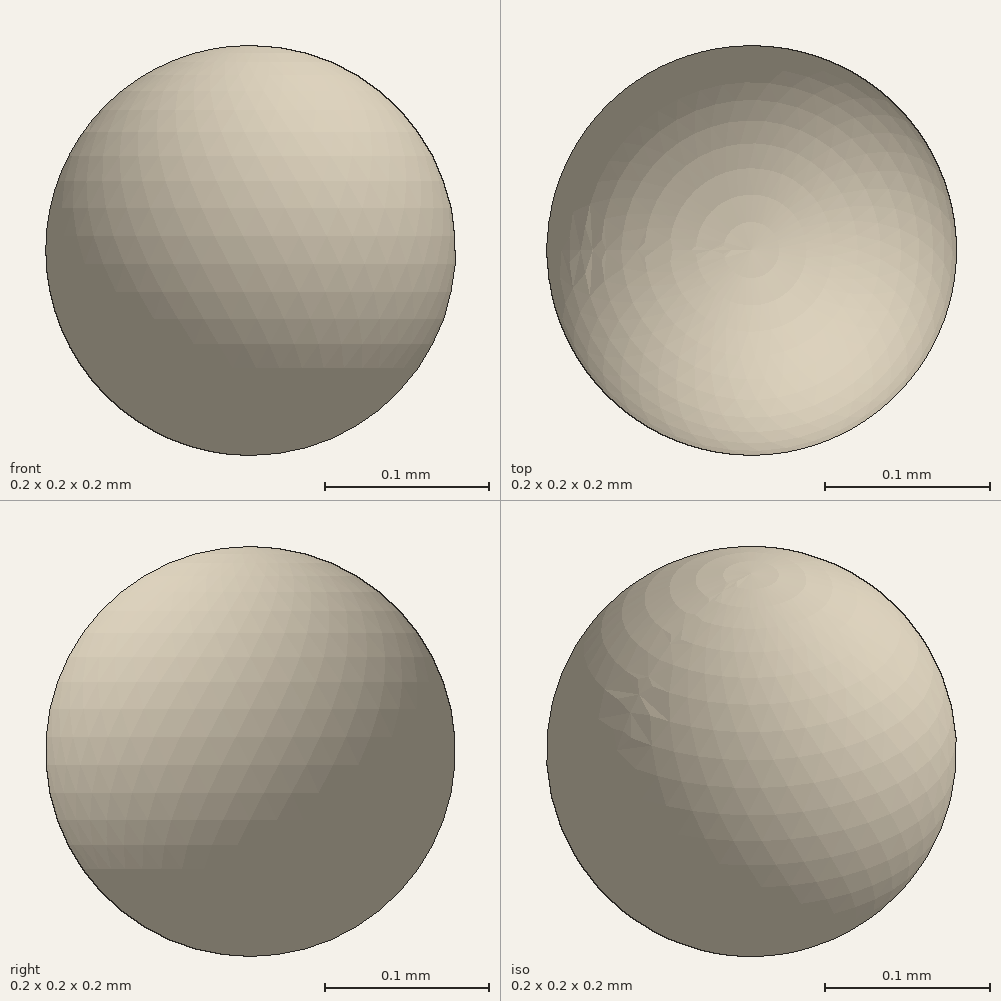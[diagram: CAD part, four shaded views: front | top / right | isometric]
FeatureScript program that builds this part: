
annotation { "Feature Type Name" : "Feature", "Feature Type Description" : "" }
export const myFeature = defineFeature(function(context is Context, id is Id, definition is map)
    precondition{}
    {
        {
            var Q0;
            Q0=qCreatedBy(makeId("Front.planeOp"),FACE);
            var sketch = newSketch(context, id + "F0", { "sketchPlane" : qUnion([Q0])});
            skCircle(sketch, "E0", {"center": v(0, 0) * mm, "radius": 0.12 * mm});
            skLineSegment(sketch, "E1", {"start": v(0, 0.12) * mm, "end": v(0, -0.12) * mm});
            skSolve(sketch);
        }
        {
            var Q0;
            {var subQ0=sQuery(id+"F0.wireOp",EDGE,"E1");Q0=makeQuery(id+"F0.imprint","IMPRINT",FACE,{"disambiguationData":[TD([[makeQuery(id+"F0.imprint","IMPRINT",EDGE,{"derivedFrom":subQ0}),1.0]])]});}
            var Q1;
            Q1=sQuery(id+"F0.wireOp",EDGE,"E1");
            revolve(context, id + "F1", {"entities" : qUnion([Q0]), "axis" : qUnion([Q1]), "revolveType" : RevolveType.FULL});
        }
    });
